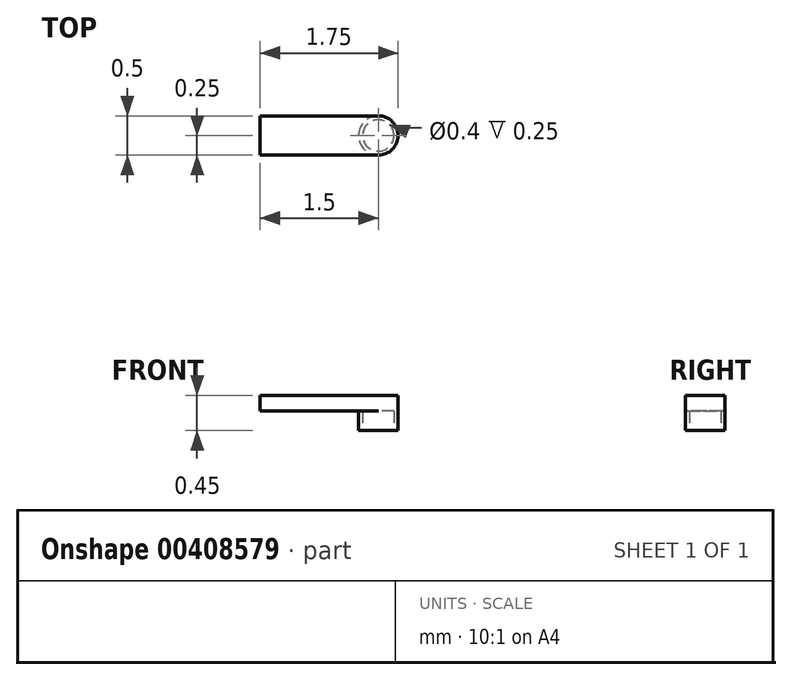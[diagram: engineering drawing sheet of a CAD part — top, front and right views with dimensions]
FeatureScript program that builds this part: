
annotation { "Feature Type Name" : "Feature", "Feature Type Description" : "" }
export const myFeature = defineFeature(function(context is Context, id is Id, definition is map)
    precondition{}
    {
        {
            var Q0;
            Q0=qCreatedBy(makeId("Top.planeOp"),FACE);
            var sketch = newSketch(context, id + "F0", { "sketchPlane" : qUnion([Q0])});
            skCircle(sketch, "E0", {"center": v(0, 0) * mm, "radius": 0.2 * mm});
            skCircle(sketch, "E1", {"center": v(0, 0) * mm, "radius": 0.25 * mm});
            skSolve(sketch);
        }
        {
            var Q0;
            Q0 = qSketchRegion(id + "F0", true);
            extrude(context, id + "F1", {"entities" : qUnion([Q0]), "depth" : 0.25 * mm});
        }
        {
            var Q0;
            Q0=makeQuery(id+"F1.opExtrude","CAP_FACE",FACE,{"disambiguationData":[OSD([sQuery(id+"F0.wireOp",EDGE,"E0"),sQuery(id+"F0.wireOp",EDGE,"E1")])],"isStart":false});
            var sketch = newSketch(context, id + "F2", { "sketchPlane" : qUnion([Q0])});
            skArc(sketch, "E2", {"start": v(0, -0.25) * mm, "mid": v(0.25, 0) * mm, "end": v(0, 0.25) * mm});
            skLineSegment(sketch, "E3", {"start": v(0, 0.25) * mm, "end": v(-1.5, 0.25) * mm});
            skLineSegment(sketch, "E4", {"start": v(0, -0.25) * mm, "end": v(-1.5, -0.25) * mm});
            skLineSegment(sketch, "E5", {"start": v(-1.5, -0.25) * mm, "end": v(-1.5, 0.25) * mm});
            skSolve(sketch);
        }
        {
            var Q0;
            Q0 = qSketchRegion(id + "F2", true);
            extrude(context, id + "F3", {"entities" : qUnion([Q0]), "operationType" : NewBodyOperationType.ADD, "depth" : 0.2 * mm, "offsetDistance" : 25 * mm});
        }
    });
